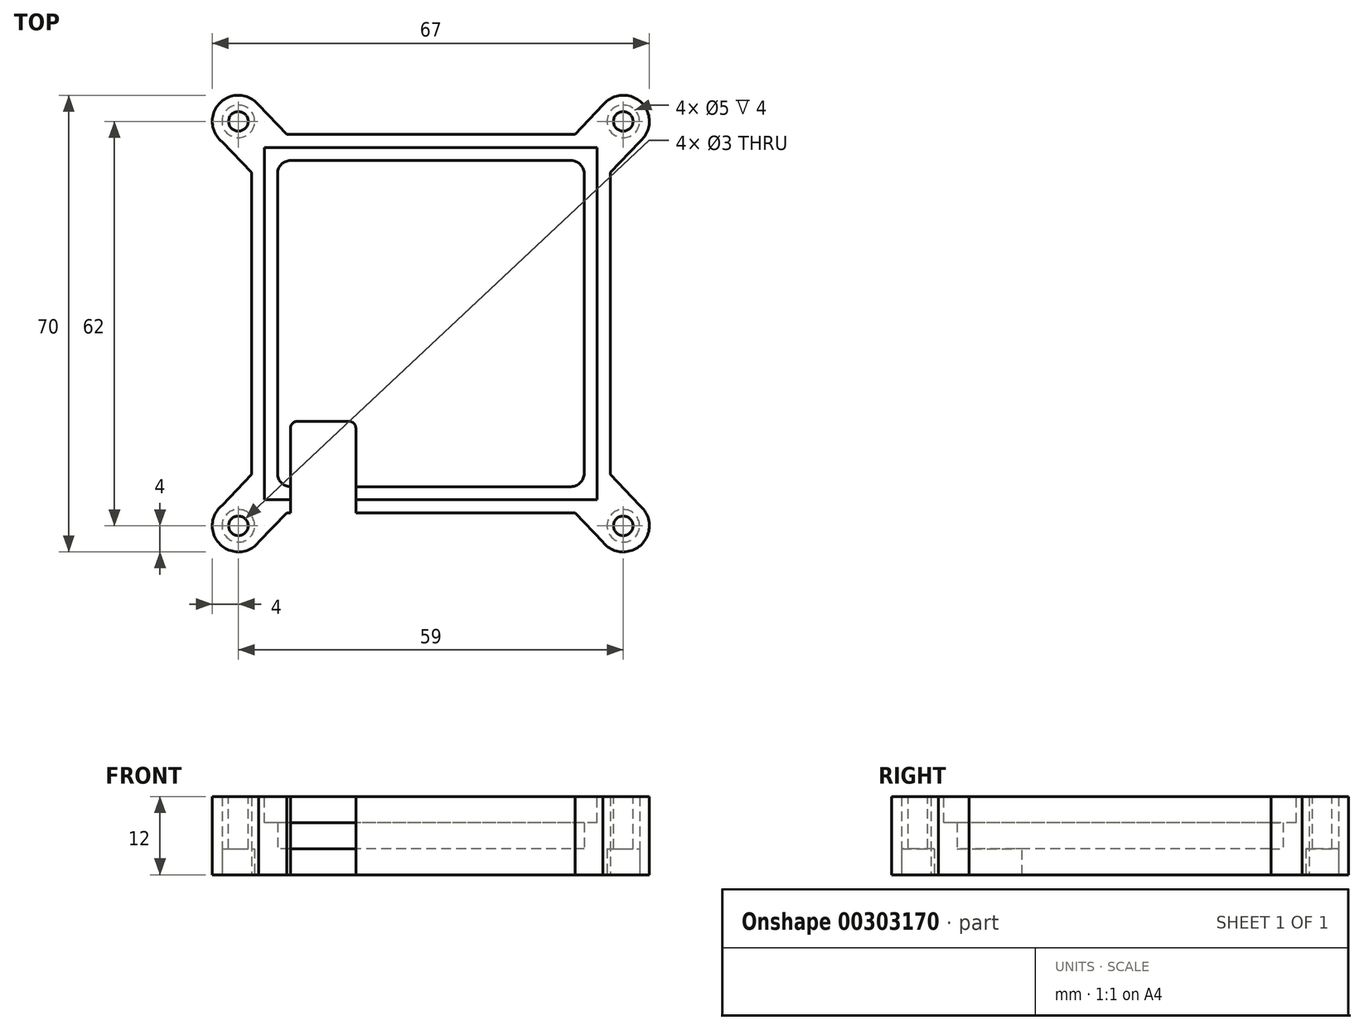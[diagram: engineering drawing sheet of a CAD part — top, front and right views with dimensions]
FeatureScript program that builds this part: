
annotation { "Feature Type Name" : "Feature", "Feature Type Description" : "" }
export const myFeature = defineFeature(function(context is Context, id is Id, definition is map)
    precondition{}
    {
        {
            var Q0;
            Q0=qCreatedBy(makeId("Top.planeOp"),FACE);
            var sketch = newSketch(context, id + "F0", { "sketchPlane" : qUnion([Q0])});
            skLineSegment(sketch, "E0.bottom", {"start": v(27.5, 29) * mm, "end": v(-27.5, 29) * mm});
            skLineSegment(sketch, "E0.top", {"start": v(27.5, -29) * mm, "end": v(-27.5, -29) * mm});
            skLineSegment(sketch, "E0.left", {"start": v(27.5, 29) * mm, "end": v(27.5, -29) * mm});
            skLineSegment(sketch, "E0.right", {"start": v(-27.5, 29) * mm, "end": v(-27.5, -29) * mm});
            skPoint(sketch, "E0.middle", {"position": v(0, 0) * mm});
            skSolve(sketch);
        }
        {
            var Q0;
            Q0=makeQuery(id+"F0.imprint","IMPRINT",FACE,{"disambiguationData":[TD([[makeQuery(id+"F0.imprint","IMPRINT",EDGE,{"derivedFrom":sQuery(id+"F0.wireOp",EDGE,"E0.bottom")}),1.0]])]});
            extrude(context, id + "F1", {"entities" : qUnion([Q0]), "depth" : 4 * mm});
        }
        {
            var Q0;
            Q0=makeQuery(id+"F1.opExtrude","CAP_FACE",FACE,{"disambiguationData":[OSD([sQuery(id+"F0.wireOp",EDGE,"E0.bottom"),sQuery(id+"F0.wireOp",EDGE,"E0.top"),sQuery(id+"F0.wireOp",EDGE,"E0.left"),sQuery(id+"F0.wireOp",EDGE,"E0.right")])],"isStart":false});
            var sketch = newSketch(context, id + "F2", { "sketchPlane" : qUnion([Q0])});
            skLineSegment(sketch, "E1.bottom", {"start": v(23.5, 25) * mm, "end": v(-23.5, 25) * mm});
            skLineSegment(sketch, "E1.top", {"start": v(23.5, -25) * mm, "end": v(-23.5, -25) * mm});
            skLineSegment(sketch, "E1.left", {"start": v(23.5, 25) * mm, "end": v(23.5, -25) * mm});
            skLineSegment(sketch, "E1.right", {"start": v(-23.5, 25) * mm, "end": v(-23.5, -25) * mm});
            skPoint(sketch, "E1.middle", {"position": v(0, 0) * mm});
            skSolve(sketch);
        }
        {
            var Q0;
            Q0=makeQuery(id+"F2.imprint","IMPRINT",FACE,{"disambiguationData":[TD([[makeQuery(id+"F2.imprint","IMPRINT",EDGE,{"derivedFrom":sQuery(id+"F2.wireOp",EDGE,"E1.bottom")}),-1.0]])]});
            extrude(context, id + "F3", {"entities" : qUnion([Q0]), "operationType" : NewBodyOperationType.ADD, "depth" : 8 * mm});
        }
        {
            var Q0;
            Q0=makeQuery(id+"F3.opExtrude","SWEPT_EDGE",EDGE,{"disambiguationData":[OSD([sQuery(id+"F2.wireOp",EDGE,"E1.top"),sQuery(id+"F2.wireOp",EDGE,"E1.left")])]});
            var Q1;
            Q1=makeQuery(id+"F3.opExtrude","SWEPT_EDGE",EDGE,{"disambiguationData":[OSD([sQuery(id+"F2.wireOp",EDGE,"E1.top"),sQuery(id+"F2.wireOp",EDGE,"E1.right")])]});
            var Q2;
            Q2=makeQuery(id+"F3.opExtrude","SWEPT_EDGE",EDGE,{"disambiguationData":[OSD([sQuery(id+"F2.wireOp",EDGE,"E1.bottom"),sQuery(id+"F2.wireOp",EDGE,"E1.right")])]});
            var Q3;
            Q3=makeQuery(id+"F3.opExtrude","SWEPT_EDGE",EDGE,{"disambiguationData":[OSD([sQuery(id+"F2.wireOp",EDGE,"E1.bottom"),sQuery(id+"F2.wireOp",EDGE,"E1.left")])]});
            fillet(context, id + "F4", {"entities" : qUnion([Q0, Q1, Q2, Q3]), "radius" : 2 * mm, "tangentPropagation" : true, "allowEdgeOverflow" : false});
        }
        {
            var Q0;
            Q0=makeQuery(id+"F3.opExtrude","CAP_FACE",FACE,{"disambiguationData":[OSD([sQuery(id+"F0.wireOp",EDGE,"E0.bottom"),sQuery(id+"F0.wireOp",EDGE,"E0.top"),sQuery(id+"F0.wireOp",EDGE,"E0.left"),sQuery(id+"F0.wireOp",EDGE,"E0.right"),sQuery(id+"F2.wireOp",EDGE,"E1.bottom"),sQuery(id+"F2.wireOp",EDGE,"E1.top"),sQuery(id+"F2.wireOp",EDGE,"E1.left"),sQuery(id+"F2.wireOp",EDGE,"E1.right")])],"isStart":false});
            var sketch = newSketch(context, id + "F5", { "sketchPlane" : qUnion([Q0])});
            skLineSegment(sketch, "E2.bottom", {"start": v(-21.5, -25) * mm, "end": v(-11.5, -25) * mm});
            skLineSegment(sketch, "E2.top", {"start": v(-21.5, -15) * mm, "end": v(-11.5, -15) * mm});
            skLineSegment(sketch, "E2.left", {"start": v(-21.5, -25) * mm, "end": v(-21.5, -15) * mm});
            skLineSegment(sketch, "E2.right", {"start": v(-11.5, -25) * mm, "end": v(-11.5, -15) * mm});
            skSolve(sketch);
        }
        {
            var Q0;
            Q0=makeQuery(id+"F5.imprint","IMPRINT",FACE,{"disambiguationData":[TD([[makeQuery(id+"F5.imprint","IMPRINT",EDGE,{"derivedFrom":sQuery(id+"F5.wireOp",EDGE,"00zraCXB-dsQK-ibw9-gbv8-YaiptSx0vhQ4.bottom")}),-1.0]])]});
            var Q1;
            Q1=makeQuery(id+"F5.imprint","IMPRINT",FACE,{"disambiguationData":[TD([[makeQuery(id+"F5.imprint","IMPRINT",EDGE,{"derivedFrom":sQuery(id+"F5.wireOp",EDGE,"E2.bottom")}),-1.0]])]});
            extrude(context, id + "F6", {"entities" : qUnion([Q0, Q1]), "operationType" : NewBodyOperationType.REMOVE, "oppositeDirection" : true, "depth" : 25.4 * mm});
        }
        {
            var Q0;
            Q0=makeQuery(id+"F3.opExtrude","CAP_FACE",FACE,{"disambiguationData":[OSD([sQuery(id+"F0.wireOp",EDGE,"E0.bottom"),sQuery(id+"F0.wireOp",EDGE,"E0.top"),sQuery(id+"F0.wireOp",EDGE,"E0.left"),sQuery(id+"F0.wireOp",EDGE,"E0.right"),sQuery(id+"F2.wireOp",EDGE,"E1.bottom"),sQuery(id+"F2.wireOp",EDGE,"E1.top"),sQuery(id+"F2.wireOp",EDGE,"E1.left"),sQuery(id+"F2.wireOp",EDGE,"E1.right")])],"isStart":false});
            var sketch = newSketch(context, id + "F7", { "sketchPlane" : qUnion([Q0])});
            skLineSegment(sketch, "E3.bottom", {"start": v(-21.5, -25) * mm, "end": v(-11.5, -25) * mm});
            skLineSegment(sketch, "E3.top", {"start": v(-21.5, -29) * mm, "end": v(-11.5, -29) * mm});
            skLineSegment(sketch, "E3.left", {"start": v(-21.5, -25) * mm, "end": v(-21.5, -29) * mm});
            skLineSegment(sketch, "E3.right", {"start": v(-11.5, -25) * mm, "end": v(-11.5, -29) * mm});
            skSolve(sketch);
        }
        {
            var Q0;
            Q0=makeQuery(id+"F7.imprint","IMPRINT",FACE,{"disambiguationData":[TD([[makeQuery(id+"F7.imprint","IMPRINT",EDGE,{"derivedFrom":sQuery(id+"F7.wireOp",EDGE,"5v3e8kUk-183W-gp0o-Dpl3-57JeppqVZIBp.bottom")}),1.0]])]});
            var Q1;
            Q1=makeQuery(id+"F7.imprint","IMPRINT",FACE,{"disambiguationData":[TD([[makeQuery(id+"F7.imprint","IMPRINT",EDGE,{"derivedFrom":sQuery(id+"F7.wireOp",EDGE,"E3.bottom")}),1.0]])]});
            extrude(context, id + "F8", {"entities" : qUnion([Q0, Q1]), "operationType" : NewBodyOperationType.REMOVE, "oppositeDirection" : true, "depth" : 17.02 * mm});
        }
        {
            var Q0;
            Q0=makeQuery(id+"F6.boolean.opBoolean","COPY",EDGE,{"derivedFrom":makeQuery(id+"F6.opExtrude","SWEPT_EDGE",EDGE,{"disambiguationData":[OSD([sQuery(id+"F5.wireOp",EDGE,"00zraCXB-dsQK-ibw9-gbv8-YaiptSx0vhQ4.top"),sQuery(id+"F5.wireOp",EDGE,"00zraCXB-dsQK-ibw9-gbv8-YaiptSx0vhQ4.right")])]})});
            var Q1;
            Q1=makeQuery(id+"F6.boolean.opBoolean","COPY",EDGE,{"derivedFrom":makeQuery(id+"F6.opExtrude","SWEPT_EDGE",EDGE,{"disambiguationData":[OSD([sQuery(id+"F5.wireOp",EDGE,"00zraCXB-dsQK-ibw9-gbv8-YaiptSx0vhQ4.top"),sQuery(id+"F5.wireOp",EDGE,"00zraCXB-dsQK-ibw9-gbv8-YaiptSx0vhQ4.left")])]})});
            var Q2;
            Q2=makeQuery(id+"F6.boolean.opBoolean","COPY",EDGE,{"derivedFrom":makeQuery(id+"F6.opExtrude","SWEPT_EDGE",EDGE,{"disambiguationData":[OSD([sQuery(id+"F5.wireOp",EDGE,"E2.top"),sQuery(id+"F5.wireOp",EDGE,"E2.left")])]})});
            var Q3;
            Q3=makeQuery(id+"F6.boolean.opBoolean","COPY",EDGE,{"derivedFrom":makeQuery(id+"F6.opExtrude","SWEPT_EDGE",EDGE,{"disambiguationData":[OSD([sQuery(id+"F5.wireOp",EDGE,"E2.top"),sQuery(id+"F5.wireOp",EDGE,"E2.right")])]})});
            fillet(context, id + "F9", {"entities" : qUnion([Q0, Q1, Q2, Q3]), "radius" : 1 * mm, "tangentPropagation" : true, "allowEdgeOverflow" : false});
        }
        {
            var Q0;
            Q0=makeQuery(id+"F3.opExtrude","CAP_FACE",FACE,{"disambiguationData":[OSD([sQuery(id+"F0.wireOp",EDGE,"E0.bottom"),sQuery(id+"F0.wireOp",EDGE,"E0.top"),sQuery(id+"F0.wireOp",EDGE,"E0.left"),sQuery(id+"F0.wireOp",EDGE,"E0.right"),sQuery(id+"F2.wireOp",EDGE,"E1.bottom"),sQuery(id+"F2.wireOp",EDGE,"E1.top"),sQuery(id+"F2.wireOp",EDGE,"E1.left"),sQuery(id+"F2.wireOp",EDGE,"E1.right")])],"isStart":false});
            var sketch = newSketch(context, id + "F10", { "sketchPlane" : qUnion([Q0])});
            skLineSegment(sketch, "E4.bottom", {"start": v(25.5, 27) * mm, "end": v(-25.5, 27) * mm});
            skLineSegment(sketch, "E4.top", {"start": v(25.5, -27) * mm, "end": v(-25.5, -27) * mm});
            skLineSegment(sketch, "E4.left", {"start": v(25.5, 27) * mm, "end": v(25.5, -27) * mm});
            skLineSegment(sketch, "E4.right", {"start": v(-25.5, 27) * mm, "end": v(-25.5, -27) * mm});
            skPoint(sketch, "E4.middle", {"position": v(0, 0) * mm});
            skSolve(sketch);
        }
        {
            var Q0;
            Q0=makeQuery(id+"F10.imprint","IMPRINT",FACE,{"disambiguationData":[TD([[makeQuery(id+"F10.imprint","IMPRINT",EDGE,{"derivedFrom":sQuery(id+"F10.wireOp",EDGE,"E4.bottom")}),1.0]])]});
            extrude(context, id + "F11", {"entities" : qUnion([Q0]), "operationType" : NewBodyOperationType.REMOVE, "oppositeDirection" : true, "depth" : 4 * mm});
        }
        {
            var Q0;
            Q0=makeQuery(id+"F1.opExtrude","CAP_FACE",FACE,{"disambiguationData":[OSD([sQuery(id+"F0.wireOp",EDGE,"E0.bottom"),sQuery(id+"F0.wireOp",EDGE,"E0.top"),sQuery(id+"F0.wireOp",EDGE,"E0.left"),sQuery(id+"F0.wireOp",EDGE,"E0.right")])],"isStart":true});
            var sketch = newSketch(context, id + "F12", { "sketchPlane" : qUnion([Q0])});
            skPoint(sketch, "E5.middle", {"position": v(0, 0) * mm});
            skCircle(sketch, "E6", {"center": v(-29.5, 31) * mm, "radius": 4 * mm});
            skCircle(sketch, "E7", {"center": v(29.5, 31) * mm, "radius": 4 * mm});
            skCircle(sketch, "E8", {"center": v(29.5, -31) * mm, "radius": 4 * mm});
            skCircle(sketch, "E9", {"center": v(-29.5, -31) * mm, "radius": 4 * mm});
            skLineSegment(sketch, "E10.bottom", {"start": v(32, 33.5) * mm, "end": v(-32, 33.5) * mm});
            skLineSegment(sketch, "E10.top", {"start": v(32, -33.5) * mm, "end": v(-32, -33.5) * mm});
            skLineSegment(sketch, "E10.left", {"start": v(32, 33.5) * mm, "end": v(32, -33.5) * mm});
            skLineSegment(sketch, "E10.right", {"start": v(-32, 33.5) * mm, "end": v(-32, -33.5) * mm});
            skLineSegment(sketch, "E11", {"start": v(-26.38, 33.5) * mm, "end": v(32, -27.88) * mm});
            skLineSegment(sketch, "E12", {"start": v(26.38, 33.5) * mm, "end": v(-32, -27.88) * mm});
            skLineSegment(sketch, "E13", {"start": v(32, 27.88) * mm, "end": v(-26.38, -33.5) * mm});
            skLineSegment(sketch, "E14", {"start": v(26.38, -33.5) * mm, "end": v(-32, 27.88) * mm});
            skSolve(sketch);
        }
        {
            var Q0;
            {var subQ3=sQuery(id+"F12.wireOp",EDGE,"E6");var subQ6=sQuery(id+"F0.wireOp",EDGE,"E0.right");var subQ10=makeQuery(id+"F1.opExtrude","CAP_EDGE",EDGE,{"disambiguationData":[OSD([subQ6])],"isStart":true});var subQ11=makeQuery(id+"F12.imprint","INTERSECT",VERTEX,{"derivedFrom":[subQ10,subQ3]});Q0=makeQuery(id+"F12.imprint","IMPRINT",FACE,{"disambiguationData":[TD([[makeQuery(id+"F12.imprint","IMPRINT",EDGE,{"disambiguationData":[TD([[subQ11,1.0]])],"derivedFrom":subQ3}),1.0]])]});}
            var Q1;
            {var subQ0=sQuery(id+"F12.wireOp",EDGE,"E10.right");var subQ3=sQuery(id+"F12.wireOp",EDGE,"E10.bottom");var subQ5=makeQuery(id+"F12.imprint","INTERSECT",VERTEX,{"derivedFrom":[subQ3,subQ0]});Q1=makeQuery(id+"F12.imprint","IMPRINT",FACE,{"disambiguationData":[TD([[makeQuery(id+"F12.imprint","IMPRINT",EDGE,{"disambiguationData":[TD([[subQ5,1.0]])],"derivedFrom":subQ3}),-1.0]])]});}
            var Q2;
            {var subQ1=sQuery(id+"F12.wireOp",EDGE,"E6");var subQ3=makeQuery(id+"F1.opExtrude","CAP_EDGE",EDGE,{"disambiguationData":[OSD([sQuery(id+"F0.wireOp",EDGE,"E0.right")])],"isStart":true});var subQ4=makeQuery(id+"F12.imprint","INTERSECT",VERTEX,{"derivedFrom":[subQ3,subQ1]});Q2=makeQuery(id+"F12.imprint","IMPRINT",FACE,{"disambiguationData":[TD([[makeQuery(id+"F12.imprint","IMPRINT",EDGE,{"disambiguationData":[TD([[subQ4,1.0]])],"derivedFrom":subQ3}),1.0]])]});}
            var Q3;
            {var subQ0=sQuery(id+"F12.wireOp",EDGE,"E11");var subQ1=sQuery(id+"F12.wireOp",EDGE,"E6");var subQ2=makeQuery(id+"F12.imprint","INTERSECT",VERTEX,{"derivedFrom":[subQ1,sQuery(id+"F12.wireOp",EDGE,"E10.bottom"),subQ0]});Q3=makeQuery(id+"F12.imprint","IMPRINT",FACE,{"disambiguationData":[TD([[makeQuery(id+"F12.imprint","IMPRINT",EDGE,{"disambiguationData":[TD([[subQ2,1.0]])],"derivedFrom":subQ1}),-1.0]])]});}
            var Q4;
            {var subQ3=sQuery(id+"F12.wireOp",EDGE,"E7");var subQ6=sQuery(id+"F0.wireOp",EDGE,"E0.left");var subQ7=makeQuery(id+"F1.opExtrude","CAP_EDGE",EDGE,{"disambiguationData":[OSD([subQ6])],"isStart":true});var subQ8=makeQuery(id+"F12.imprint","INTERSECT",VERTEX,{"derivedFrom":[subQ7,subQ3]});Q4=makeQuery(id+"F12.imprint","IMPRINT",FACE,{"disambiguationData":[TD([[makeQuery(id+"F12.imprint","IMPRINT",EDGE,{"disambiguationData":[TD([[subQ8,-1.0]])],"derivedFrom":subQ3}),1.0]])]});}
            var Q5;
            {var subQ0=sQuery(id+"F12.wireOp",EDGE,"E10.bottom");var subQ3=sQuery(id+"F12.wireOp",EDGE,"E10.left");var subQ5=makeQuery(id+"F12.imprint","INTERSECT",VERTEX,{"derivedFrom":[subQ0,subQ3]});Q5=makeQuery(id+"F12.imprint","IMPRINT",FACE,{"disambiguationData":[TD([[makeQuery(id+"F12.imprint","IMPRINT",EDGE,{"disambiguationData":[TD([[subQ5,-1.0]])],"derivedFrom":subQ0}),-1.0]])]});}
            var Q6;
            {var subQ1=sQuery(id+"F12.wireOp",EDGE,"E7");var subQ3=makeQuery(id+"F1.opExtrude","CAP_EDGE",EDGE,{"disambiguationData":[OSD([sQuery(id+"F0.wireOp",EDGE,"E0.left")])],"isStart":true});var subQ4=makeQuery(id+"F12.imprint","INTERSECT",VERTEX,{"derivedFrom":[subQ3,subQ1]});Q6=makeQuery(id+"F12.imprint","IMPRINT",FACE,{"disambiguationData":[TD([[makeQuery(id+"F12.imprint","IMPRINT",EDGE,{"disambiguationData":[TD([[subQ4,1.0]])],"derivedFrom":subQ3}),-1.0]])]});}
            var Q7;
            {var subQ0=sQuery(id+"F12.wireOp",EDGE,"E12");var subQ1=sQuery(id+"F12.wireOp",EDGE,"E7");var subQ2=makeQuery(id+"F12.imprint","INTERSECT",VERTEX,{"derivedFrom":[subQ1,sQuery(id+"F12.wireOp",EDGE,"E10.bottom"),subQ0]});Q7=makeQuery(id+"F12.imprint","IMPRINT",FACE,{"disambiguationData":[TD([[makeQuery(id+"F12.imprint","IMPRINT",EDGE,{"disambiguationData":[TD([[subQ2,-1.0]])],"derivedFrom":subQ1}),-1.0]])]});}
            var Q8;
            {var subQ5=makeQuery(id+"F1.opExtrude","CAP_EDGE",EDGE,{"disambiguationData":[OSD([sQuery(id+"F0.wireOp",EDGE,"E0.bottom")])],"isStart":true});var subQ7=makeQuery(id+"F1.opExtrude","CAP_EDGE",EDGE,{"disambiguationData":[OSD([sQuery(id+"F0.wireOp",EDGE,"E0.right")])],"isStart":true});var subQ8=makeQuery(id+"F12.imprint","INTERSECT",VERTEX,{"derivedFrom":[subQ5,subQ7]});Q8=makeQuery(id+"F12.imprint","IMPRINT",FACE,{"disambiguationData":[TD([[makeQuery(id+"F12.imprint","IMPRINT",EDGE,{"disambiguationData":[TD([[subQ8,1.0]])],"derivedFrom":subQ5}),1.0]])]});}
            var Q9;
            {var subQ0=sQuery(id+"F12.wireOp",EDGE,"E10.right");var subQ3=sQuery(id+"F12.wireOp",EDGE,"E10.top");var subQ5=makeQuery(id+"F12.imprint","INTERSECT",VERTEX,{"derivedFrom":[subQ3,subQ0]});Q9=makeQuery(id+"F12.imprint","IMPRINT",FACE,{"disambiguationData":[TD([[makeQuery(id+"F12.imprint","IMPRINT",EDGE,{"disambiguationData":[TD([[subQ5,1.0]])],"derivedFrom":subQ3}),1.0]])]});}
            var Q10;
            {var subQ1=sQuery(id+"F12.wireOp",EDGE,"E9");var subQ3=makeQuery(id+"F1.opExtrude","CAP_EDGE",EDGE,{"disambiguationData":[OSD([sQuery(id+"F0.wireOp",EDGE,"E0.right")])],"isStart":true});var subQ4=makeQuery(id+"F12.imprint","INTERSECT",VERTEX,{"derivedFrom":[subQ3,subQ1]});Q10=makeQuery(id+"F12.imprint","IMPRINT",FACE,{"disambiguationData":[TD([[makeQuery(id+"F12.imprint","IMPRINT",EDGE,{"disambiguationData":[TD([[subQ4,-1.0]])],"derivedFrom":subQ3}),1.0]])]});}
            var Q11;
            {var subQ1=sQuery(id+"F12.wireOp",EDGE,"E9");var subQ3=makeQuery(id+"F1.opExtrude","CAP_EDGE",EDGE,{"disambiguationData":[OSD([sQuery(id+"F0.wireOp",EDGE,"E0.bottom")])],"isStart":true});var subQ4=makeQuery(id+"F12.imprint","INTERSECT",VERTEX,{"derivedFrom":[subQ3,subQ1]});Q11=makeQuery(id+"F12.imprint","IMPRINT",FACE,{"disambiguationData":[TD([[makeQuery(id+"F12.imprint","IMPRINT",EDGE,{"disambiguationData":[TD([[subQ4,1.0]])],"derivedFrom":subQ3}),1.0]])]});}
            var Q12;
            {var subQ1=sQuery(id+"F12.wireOp",EDGE,"E10.top");var subQ3=sQuery(id+"F12.wireOp",EDGE,"E8");var subQ4=makeQuery(id+"F12.imprint","INTERSECT",VERTEX,{"derivedFrom":[subQ3,subQ1]});Q12=makeQuery(id+"F12.imprint","IMPRINT",FACE,{"disambiguationData":[TD([[makeQuery(id+"F12.imprint","IMPRINT",EDGE,{"disambiguationData":[TD([[subQ4,1.0]])],"derivedFrom":subQ3}),1.0]])]});}
            var Q13;
            {var subQ0=sQuery(id+"F12.wireOp",EDGE,"E10.top");var subQ1=sQuery(id+"F12.wireOp",EDGE,"E8");var subQ2=makeQuery(id+"F12.imprint","INTERSECT",VERTEX,{"derivedFrom":[subQ1,subQ0]});Q13=makeQuery(id+"F12.imprint","IMPRINT",FACE,{"disambiguationData":[TD([[makeQuery(id+"F12.imprint","IMPRINT",EDGE,{"disambiguationData":[TD([[subQ2,1.0]])],"derivedFrom":subQ1}),-1.0]])]});}
            var Q14;
            {var subQ1=sQuery(id+"F12.wireOp",EDGE,"E8");var subQ3=makeQuery(id+"F1.opExtrude","CAP_EDGE",EDGE,{"disambiguationData":[OSD([sQuery(id+"F0.wireOp",EDGE,"E0.left")])],"isStart":true});var subQ4=makeQuery(id+"F12.imprint","INTERSECT",VERTEX,{"derivedFrom":[subQ3,subQ1]});Q14=makeQuery(id+"F12.imprint","IMPRINT",FACE,{"disambiguationData":[TD([[makeQuery(id+"F12.imprint","IMPRINT",EDGE,{"disambiguationData":[TD([[subQ4,-1.0]])],"derivedFrom":subQ3}),-1.0]])]});}
            var Q15;
            {var subQ0=sQuery(id+"F12.wireOp",EDGE,"E10.left");var subQ3=sQuery(id+"F12.wireOp",EDGE,"E10.top");var subQ5=makeQuery(id+"F12.imprint","INTERSECT",VERTEX,{"derivedFrom":[subQ3,subQ0]});Q15=makeQuery(id+"F12.imprint","IMPRINT",FACE,{"disambiguationData":[TD([[makeQuery(id+"F12.imprint","IMPRINT",EDGE,{"disambiguationData":[TD([[subQ5,-1.0]])],"derivedFrom":subQ3}),1.0]])]});}
            extrude(context, id + "F13", {"entities" : qUnion([Q0, Q1, Q2, Q3, Q4, Q5, Q6, Q7, Q8, Q9, Q10, Q11, Q12, Q13, Q14, Q15]), "operationType" : NewBodyOperationType.ADD, "oppositeDirection" : true, "depth" : 12 * mm});
        }
        {
            var Q0;
            {var subQ0=sQuery(id+"F12.wireOp",EDGE,"E13");var subQ1=sQuery(id+"F12.wireOp",EDGE,"E12");var subQ2=sQuery(id+"F0.wireOp",EDGE,"E0.right");var subQ3=sQuery(id+"F0.wireOp",EDGE,"E0.bottom");var subQ4=sQuery(id+"F12.wireOp",EDGE,"E14");var subQ5=sQuery(id+"F12.wireOp",EDGE,"E11");var subQ6=sQuery(id+"F0.wireOp",EDGE,"E0.left");var subQ7=sQuery(id+"F0.wireOp",EDGE,"E0.top");Q0=makeQuery(id+"F13.boolean.opBoolean","MERGE",FACE,{"derivedFrom":[makeQuery(id+"F1.opExtrude","CAP_FACE",FACE,{"disambiguationData":[OSD([subQ3,subQ7,subQ6,subQ2])],"isStart":true}),makeQuery(id+"F13.opExtrude","CAP_FACE",FACE,{"disambiguationData":[OSD([subQ7,subQ2,sQuery(id+"F12.wireOp",EDGE,"E6"),subQ5,subQ4])],"isStart":true}),makeQuery(id+"F13.opExtrude","CAP_FACE",FACE,{"disambiguationData":[OSD([subQ7,subQ6,sQuery(id+"F12.wireOp",EDGE,"E7"),subQ1,subQ0])],"isStart":true}),makeQuery(id+"F13.opExtrude","CAP_FACE",FACE,{"disambiguationData":[OSD([subQ3,subQ6,sQuery(id+"F12.wireOp",EDGE,"E8"),subQ5,subQ4])],"isStart":true}),makeQuery(id+"F13.opExtrude","CAP_FACE",FACE,{"disambiguationData":[OSD([subQ3,subQ2,sQuery(id+"F12.wireOp",EDGE,"E9"),subQ1,subQ0])],"isStart":true})]});}
            var sketch = newSketch(context, id + "F14", { "sketchPlane" : qUnion([Q0])});
            skCircle(sketch, "E15", {"center": v(29.5, 31) * mm, "radius": 2.5 * mm});
            skCircle(sketch, "E16", {"center": v(29.5, -31) * mm, "radius": 2.5 * mm});
            skCircle(sketch, "E17", {"center": v(-29.5, -31) * mm, "radius": 2.5 * mm});
            skCircle(sketch, "E18", {"center": v(-29.5, 31) * mm, "radius": 2.5 * mm});
            skSolve(sketch);
        }
        {
            var Q0;
            Q0=makeQuery(id+"F14.imprint","IMPRINT",FACE,{"disambiguationData":[TD([[makeQuery(id+"F14.imprint","IMPRINT",EDGE,{"derivedFrom":sQuery(id+"F14.wireOp",EDGE,"E17")}),1.0]])]});
            var Q1;
            Q1=makeQuery(id+"F14.imprint","IMPRINT",FACE,{"disambiguationData":[TD([[makeQuery(id+"F14.imprint","IMPRINT",EDGE,{"derivedFrom":sQuery(id+"F14.wireOp",EDGE,"E16")}),1.0]])]});
            var Q2;
            Q2=makeQuery(id+"F14.imprint","IMPRINT",FACE,{"disambiguationData":[TD([[makeQuery(id+"F14.imprint","IMPRINT",EDGE,{"derivedFrom":sQuery(id+"F14.wireOp",EDGE,"E18")}),1.0]])]});
            var Q3;
            Q3=makeQuery(id+"F14.imprint","IMPRINT",FACE,{"disambiguationData":[TD([[makeQuery(id+"F14.imprint","IMPRINT",EDGE,{"derivedFrom":sQuery(id+"F14.wireOp",EDGE,"E15")}),1.0]])]});
            extrude(context, id + "F15", {"entities" : qUnion([Q0, Q1, Q2, Q3]), "operationType" : NewBodyOperationType.REMOVE, "oppositeDirection" : true, "depth" : 4 * mm});
        }
        {
            var Q0;
            {var subQ0=sQuery(id+"F12.wireOp",EDGE,"E13");var subQ1=sQuery(id+"F12.wireOp",EDGE,"E12");var subQ2=sQuery(id+"F0.wireOp",EDGE,"E0.right");var subQ3=sQuery(id+"F0.wireOp",EDGE,"E0.bottom");var subQ4=sQuery(id+"F12.wireOp",EDGE,"E14");var subQ5=sQuery(id+"F12.wireOp",EDGE,"E11");var subQ6=sQuery(id+"F0.wireOp",EDGE,"E0.left");var subQ7=sQuery(id+"F0.wireOp",EDGE,"E0.top");Q0=makeQuery(id+"F13.boolean.opBoolean","MERGE",FACE,{"derivedFrom":[makeQuery(id+"F3.opExtrude","CAP_FACE",FACE,{"disambiguationData":[OSD([subQ3,subQ7,subQ6,subQ2,sQuery(id+"F2.wireOp",EDGE,"E1.bottom"),sQuery(id+"F2.wireOp",EDGE,"E1.top"),sQuery(id+"F2.wireOp",EDGE,"E1.left"),sQuery(id+"F2.wireOp",EDGE,"E1.right")])],"isStart":false}),makeQuery(id+"F13.opExtrude","CAP_FACE",FACE,{"disambiguationData":[OSD([subQ7,subQ2,sQuery(id+"F12.wireOp",EDGE,"E6"),subQ5,subQ4])],"isStart":false}),makeQuery(id+"F13.opExtrude","CAP_FACE",FACE,{"disambiguationData":[OSD([subQ7,subQ6,sQuery(id+"F12.wireOp",EDGE,"E7"),subQ1,subQ0])],"isStart":false}),makeQuery(id+"F13.opExtrude","CAP_FACE",FACE,{"disambiguationData":[OSD([subQ3,subQ6,sQuery(id+"F12.wireOp",EDGE,"E8"),subQ5,subQ4])],"isStart":false}),makeQuery(id+"F13.opExtrude","CAP_FACE",FACE,{"disambiguationData":[OSD([subQ3,subQ2,sQuery(id+"F12.wireOp",EDGE,"E9"),subQ1,subQ0])],"isStart":false})]});}
            var sketch = newSketch(context, id + "F16", { "sketchPlane" : qUnion([Q0])});
            skCircle(sketch, "E19", {"center": v(29.5, -31) * mm, "radius": 1.5 * mm});
            skCircle(sketch, "E20", {"center": v(-29.5, -31) * mm, "radius": 1.5 * mm});
            skCircle(sketch, "E21", {"center": v(29.5, 31) * mm, "radius": 1.5 * mm});
            skCircle(sketch, "E22", {"center": v(-29.5, 31) * mm, "radius": 1.5 * mm});
            skSolve(sketch);
        }
        {
            var Q0;
            Q0=makeQuery(id+"F16.imprint","IMPRINT",FACE,{"disambiguationData":[TD([[makeQuery(id+"F16.imprint","IMPRINT",EDGE,{"derivedFrom":sQuery(id+"F16.wireOp",EDGE,"E19")}),1.0]])]});
            var Q1;
            Q1=makeQuery(id+"F16.imprint","IMPRINT",FACE,{"disambiguationData":[TD([[makeQuery(id+"F16.imprint","IMPRINT",EDGE,{"derivedFrom":sQuery(id+"F16.wireOp",EDGE,"E20")}),1.0]])]});
            var Q2;
            Q2=makeQuery(id+"F16.imprint","IMPRINT",FACE,{"disambiguationData":[TD([[makeQuery(id+"F16.imprint","IMPRINT",EDGE,{"derivedFrom":sQuery(id+"F16.wireOp",EDGE,"E21")}),1.0]])]});
            var Q3;
            Q3=makeQuery(id+"F16.imprint","IMPRINT",FACE,{"disambiguationData":[TD([[makeQuery(id+"F16.imprint","IMPRINT",EDGE,{"derivedFrom":sQuery(id+"F16.wireOp",EDGE,"E22")}),1.0]])]});
            extrude(context, id + "F17", {"entities" : qUnion([Q0, Q1, Q2, Q3]), "operationType" : NewBodyOperationType.REMOVE, "oppositeDirection" : true, "depth" : 25.4 * mm});
        }
    });
